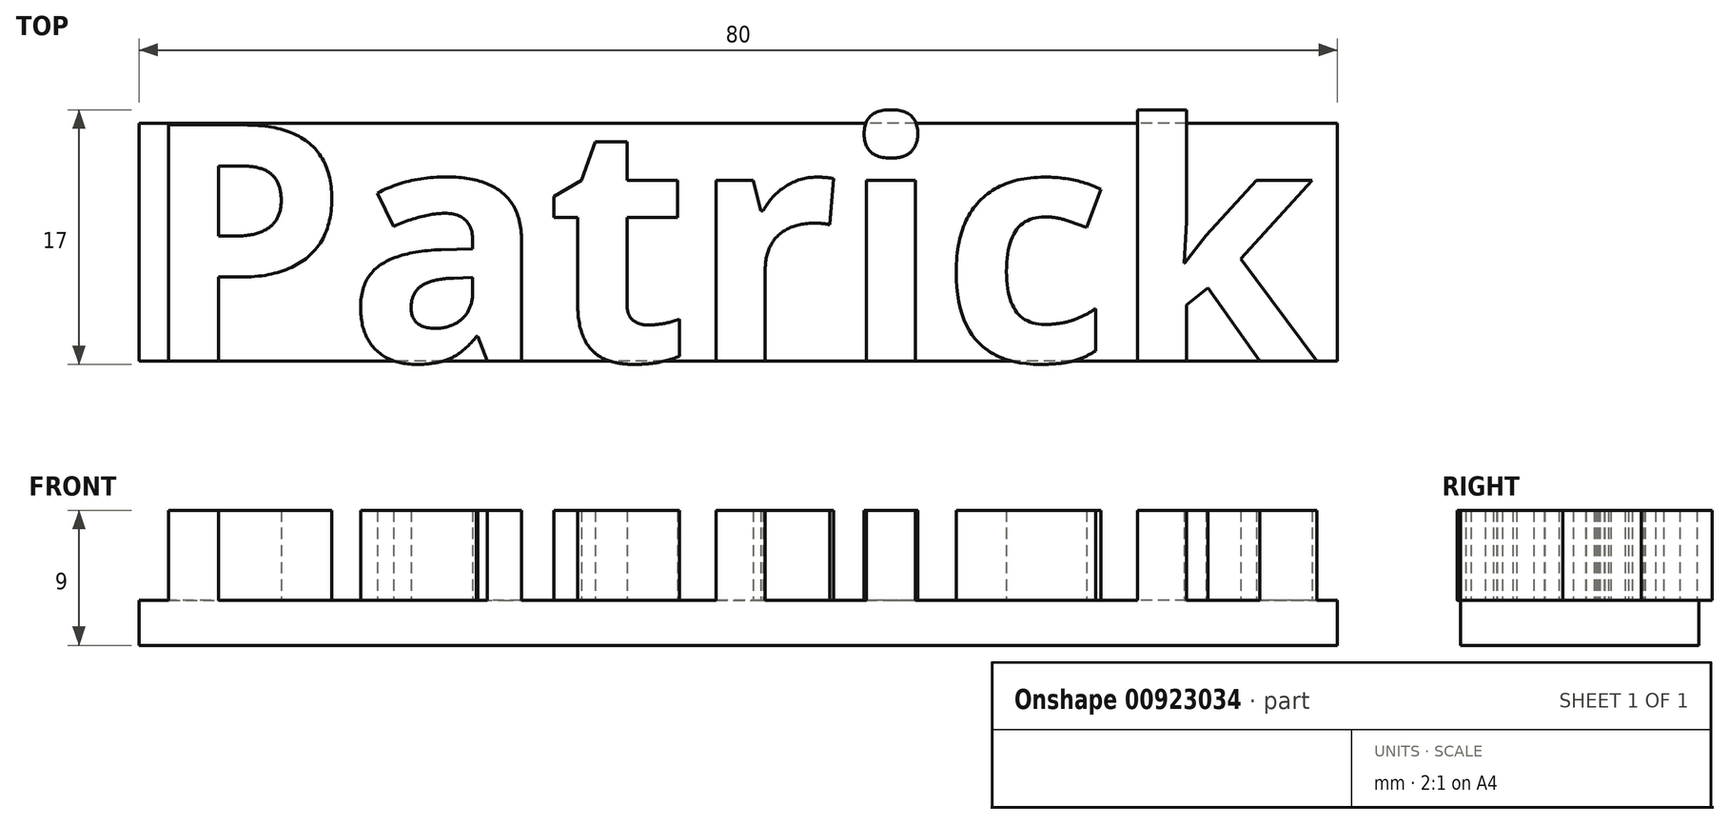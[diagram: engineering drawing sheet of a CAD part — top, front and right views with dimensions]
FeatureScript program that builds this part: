
annotation { "Feature Type Name" : "Feature", "Feature Type Description" : "" }
export const myFeature = defineFeature(function(context is Context, id is Id, definition is map)
    precondition{}
    {
        {
            var Q0;
            Q0=qCreatedBy(makeId("Top.planeOp"),FACE);
            var sketch = newSketch(context, id + "F0", { "sketchPlane" : qUnion([Q0])});
            skText(sketch, "E0", { "text": "Patrick", "fontName": "OpenSans-Bold.ttf"});
            const initialGuessF0  = {"E0": [-0.01514, -0.00767, 1, 0, 0.0159]};
            skSetInitialGuess(sketch, initialGuessF0);
            skSolve(sketch);
        }
        {
            var Q0;
            Q0=qCreatedBy(makeId("Top.planeOp"),FACE);
            var sketch = newSketch(context, id + "F1", { "sketchPlane" : qUnion([Q0])});
            skLineSegment(sketch, "E1.bottom", {"start": v(64.86, 8.22) * mm, "end": v(-15.14, 8.22) * mm});
            skLineSegment(sketch, "E1.top", {"start": v(64.86, -7.67) * mm, "end": v(-15.14, -7.67) * mm});
            skLineSegment(sketch, "E1.left", {"start": v(64.86, 8.22) * mm, "end": v(64.86, -7.67) * mm});
            skLineSegment(sketch, "E1.right", {"start": v(-15.14, 8.22) * mm, "end": v(-15.14, -7.67) * mm});
            skSolve(sketch);
        }
        {
            var Q0;
            Q0 = qSketchRegion(id + "F1", true);
            extrude(context, id + "F2", {"entities" : qUnion([Q0]), "oppositeDirection" : true, "depth" : 3 * mm, "offsetDistance" : 25 * mm});
        }
        {
            var Q0;
            Q0 = qSketchRegion(id + "F0", true);
            extrude(context, id + "F3", {"entities" : qUnion([Q0]), "operationType" : NewBodyOperationType.ADD, "depth" : 6 * mm, "offsetDistance" : 25 * mm});
        }
    });
